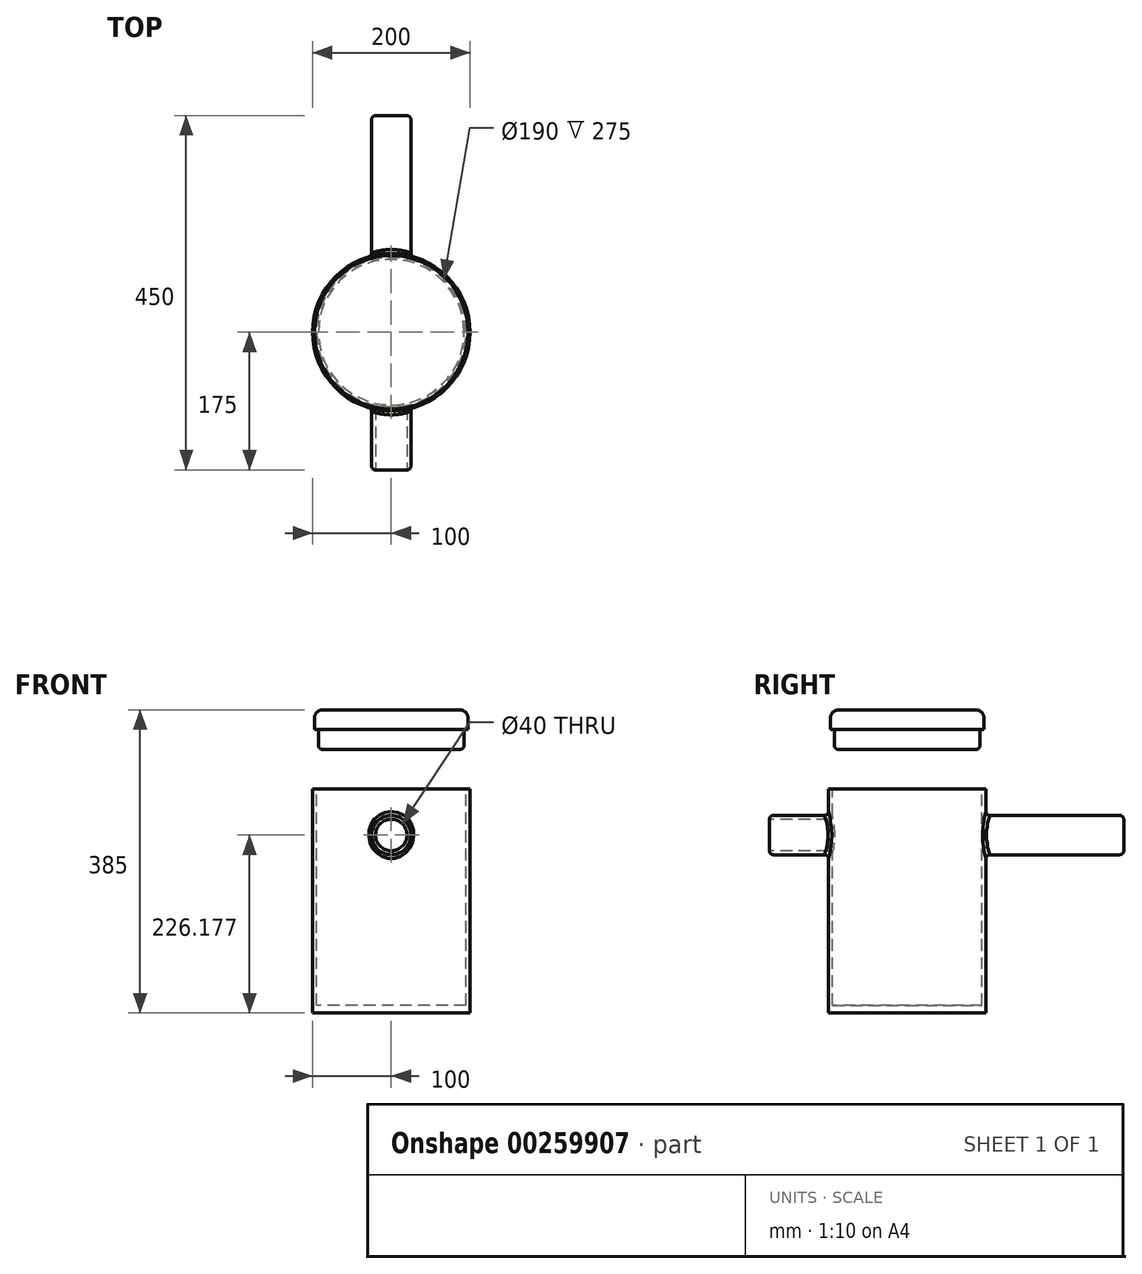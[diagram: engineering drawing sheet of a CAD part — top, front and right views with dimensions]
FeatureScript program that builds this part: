
annotation { "Feature Type Name" : "Feature", "Feature Type Description" : "" }
export const myFeature = defineFeature(function(context is Context, id is Id, definition is map)
    precondition{}
    {
        {
            var Q0;
            Q0=qCreatedBy(makeId("Top.planeOp"),FACE);
            var sketch = newSketch(context, id + "F0", { "sketchPlane" : qUnion([Q0])});
            skCircle(sketch, "E0", {"center": v(0, 0) * mm, "radius": 100 * mm});
            skSolve(sketch);
        }
        {
            var Q0;
            Q0 = qSketchRegion(id + "F0", true);
            extrude(context, id + "F1", {"entities" : qUnion([Q0]), "depth" : 285 * mm});
        }
        {
            var Q0;
            Q0=makeQuery(id+"F1.opExtrude","CAP_FACE",FACE,{"disambiguationData":[OSD([sQuery(id+"F0.wireOp",EDGE,"E0")])],"isStart":false});
            var sketch = newSketch(context, id + "F2", { "sketchPlane" : qUnion([Q0])});
            skCircle(sketch, "E1.0", {"center": v(0, 0) * mm, "radius": 95 * mm});
            skSolve(sketch);
        }
        {
            var Q0;
            Q0=qCreatedBy(makeId("Front.planeOp"),FACE);
            var sketch = newSketch(context, id + "F3", { "sketchPlane" : qUnion([Q0])});
            skCircle(sketch, "E2", {"center": v(0, 226.18) * mm, "radius": 25 * mm});
            skSolve(sketch);
        }
        {
            var Q0;
            Q0 = qSketchRegion(id + "F3", true);
            extrude(context, id + "F4", {"entities" : qUnion([Q0]), "operationType" : NewBodyOperationType.ADD, "depth" : 175 * mm, "hasSecondDirection" : true, "secondDirectionOppositeDirection" : true, "secondDirectionDepth" : 275 * mm});
        }
        {
            var Q0;
            Q0=makeQuery(id+"F4.opExtrude","CAP_FACE",FACE,{"disambiguationData":[OSD([sQuery(id+"F3.wireOp",EDGE,"E2")])],"isStart":false});
            var sketch = newSketch(context, id + "F5", { "sketchPlane" : qUnion([Q0])});
            skCircle(sketch, "E3.0", {"center": v(0, 226.18) * mm, "radius": 20 * mm});
            skSolve(sketch);
        }
        {
            var Q0;
            Q0=makeQuery(id+"F5.imprint","IMPRINT",FACE,{"disambiguationData":[TD([[makeQuery(id+"F5.imprint","IMPRINT",EDGE,{"derivedFrom":sQuery(id+"F5.wireOp",EDGE,"E3.0")}),1.0]])]});
            extrude(context, id + "F6", {"entities" : qUnion([Q0]), "operationType" : NewBodyOperationType.REMOVE, "endBound" : BoundingType.THROUGH_ALL, "oppositeDirection" : true, "depth" : 25 * mm});
        }
        {
            var Q0;
            Q0=makeQuery(id+"F1.opExtrude","CAP_FACE",FACE,{"disambiguationData":[OSD([sQuery(id+"F0.wireOp",EDGE,"E0")])],"isStart":false});
            var sketch = newSketch(context, id + "F7", { "sketchPlane" : qUnion([Q0])});
            skCircle(sketch, "E4", {"center": v(0, 0) * mm, "radius": 92.5 * mm});
            skSolve(sketch);
        }
        {
            var Q0;
            Q0 = qSketchRegion(id + "F7", true);
            extrude(context, id + "F8", {"entities" : qUnion([Q0]), "depth" : 25 * mm});
        }
        {
            var Q0;
            Q0=makeQuery(id+"F8.opExtrude","CAP_FACE",FACE,{"disambiguationData":[OSD([sQuery(id+"F7.wireOp",EDGE,"E4")])],"isStart":false});
            var sketch = newSketch(context, id + "F9", { "sketchPlane" : qUnion([Q0])});
            skCircle(sketch, "E5", {"center": v(0, 0) * mm, "radius": 97.5 * mm});
            skSolve(sketch);
        }
        {
            var Q0;
            Q0 = qSketchRegion(id + "F9", true);
            extrude(context, id + "F10", {"entities" : qUnion([Q0]), "operationType" : NewBodyOperationType.ADD, "depth" : 25 * mm});
        }
        {
            var Q0;
            Q0=makeQuery(id+"F10.opExtrude","CAP_EDGE",EDGE,{"disambiguationData":[OSD([sQuery(id+"F9.wireOp",EDGE,"E5")])],"isStart":false});
            fillet(context, id + "F11", {"entities" : qUnion([Q0]), "radius" : 10 * mm, "tangentPropagation" : true, "allowEdgeOverflow" : false});
        }
        {
            var Q0;
            Q0=makeQuery(id+"F8.opExtrude","SWEPT_BODY",BODY,{"disambiguationData":[OSD([sQuery(id+"F7.wireOp",EDGE,"E4")])]});
            transform(context, id + "F12", {"entities" : qUnion([Q0]), "transformType" : TransformType.TRANSLATION_3D, "dx" : 0 * mm, "dy" : 0 * mm, "dz" : 50 * mm, "makeCopy" : false});
        }
        {
            var Q0;
            Q0=makeQuery(id+"F4.opExtrude","CAP_FACE",FACE,{"disambiguationData":[OSD([sQuery(id+"F3.wireOp",EDGE,"E2")])],"isStart":true});
            var sketch = newSketch(context, id + "F13", { "sketchPlane" : qUnion([Q0])});
            skCircle(sketch, "E6", {"center": v(0, 226.18) * mm, "radius": 20.05 * mm});
            skSolve(sketch);
        }
        {
            var Q0;
            Q0 = qSketchRegion(id + "F13", true);
            extrude(context, id + "F14", {"entities" : qUnion([Q0]), "operationType" : NewBodyOperationType.ADD, "oppositeDirection" : true, "depth" : 200 * mm});
        }
        {
            var Q0;
            Q0 = qSketchRegion(id + "F2", true);
            extrude(context, id + "F15", {"entities" : qUnion([Q0]), "operationType" : NewBodyOperationType.REMOVE, "oppositeDirection" : true, "depth" : 275 * mm});
        }
        {
            var Q0;
            Q0=makeQuery(id+"F4.opExtrude","CAP_EDGE",EDGE,{"disambiguationData":[OSD([sQuery(id+"F3.wireOp",EDGE,"E2")])],"isStart":false});
            var Q1;
            Q1=makeQuery(id+"F4.boolean.opBoolean","INTERSECT",EDGE,{"disambiguationData":[OD(1.0)],"derivedFrom":[makeQuery(id+"F1.opExtrude","SWEPT_FACE",FACE,{"disambiguationData":[OSD([sQuery(id+"F0.wireOp",EDGE,"E0")])]}),makeQuery(id+"F4.opExtrude","SWEPT_FACE",FACE,{"disambiguationData":[OSD([sQuery(id+"F3.wireOp",EDGE,"E2")])]})]});
            var Q2;
            Q2=makeQuery(id+"F4.boolean.opBoolean","INTERSECT",EDGE,{"disambiguationData":[OD(0.0)],"derivedFrom":[makeQuery(id+"F1.opExtrude","SWEPT_FACE",FACE,{"disambiguationData":[OSD([sQuery(id+"F0.wireOp",EDGE,"E0")])]}),makeQuery(id+"F4.opExtrude","SWEPT_FACE",FACE,{"disambiguationData":[OSD([sQuery(id+"F3.wireOp",EDGE,"E2")])]})]});
            var Q3;
            Q3=makeQuery(id+"F4.opExtrude","CAP_EDGE",EDGE,{"disambiguationData":[OSD([sQuery(id+"F3.wireOp",EDGE,"E2")])],"isStart":true});
            fillet(context, id + "F16", {"entities" : qUnion([Q0, Q1, Q2, Q3]), "radius" : 5 * mm, "tangentPropagation" : true, "allowEdgeOverflow" : false});
        }
        {
            var Q0;
            Q0=makeQuery(id+"F15.boolean.opBoolean","INTERSECT",EDGE,{"derivedFrom":[makeQuery(id+"F6.boolean.opBoolean","COPY",FACE,{"derivedFrom":makeQuery(id+"F6.opExtrude","SWEPT_FACE",FACE,{"disambiguationData":[OSD([sQuery(id+"F5.wireOp",EDGE,"E3.0")])]})}),makeQuery(id+"F15.opExtrude","SWEPT_FACE",FACE,{"disambiguationData":[OSD([sQuery(id+"F2.wireOp",EDGE,"E1.0")])]})]});
            fillet(context, id + "F17", {"entities" : qUnion([Q0]), "radius" : 5 * mm, "tangentPropagation" : true, "allowEdgeOverflow" : false});
        }
        {
            var Q0;
            Q0=makeQuery(id+"F8.opExtrude","CAP_EDGE",EDGE,{"disambiguationData":[OSD([sQuery(id+"F7.wireOp",EDGE,"E4")])],"isStart":true});
            fillet(context, id + "F18", {"entities" : qUnion([Q0]), "radius" : 5 * mm, "tangentPropagation" : true, "allowEdgeOverflow" : false});
        }
    });
